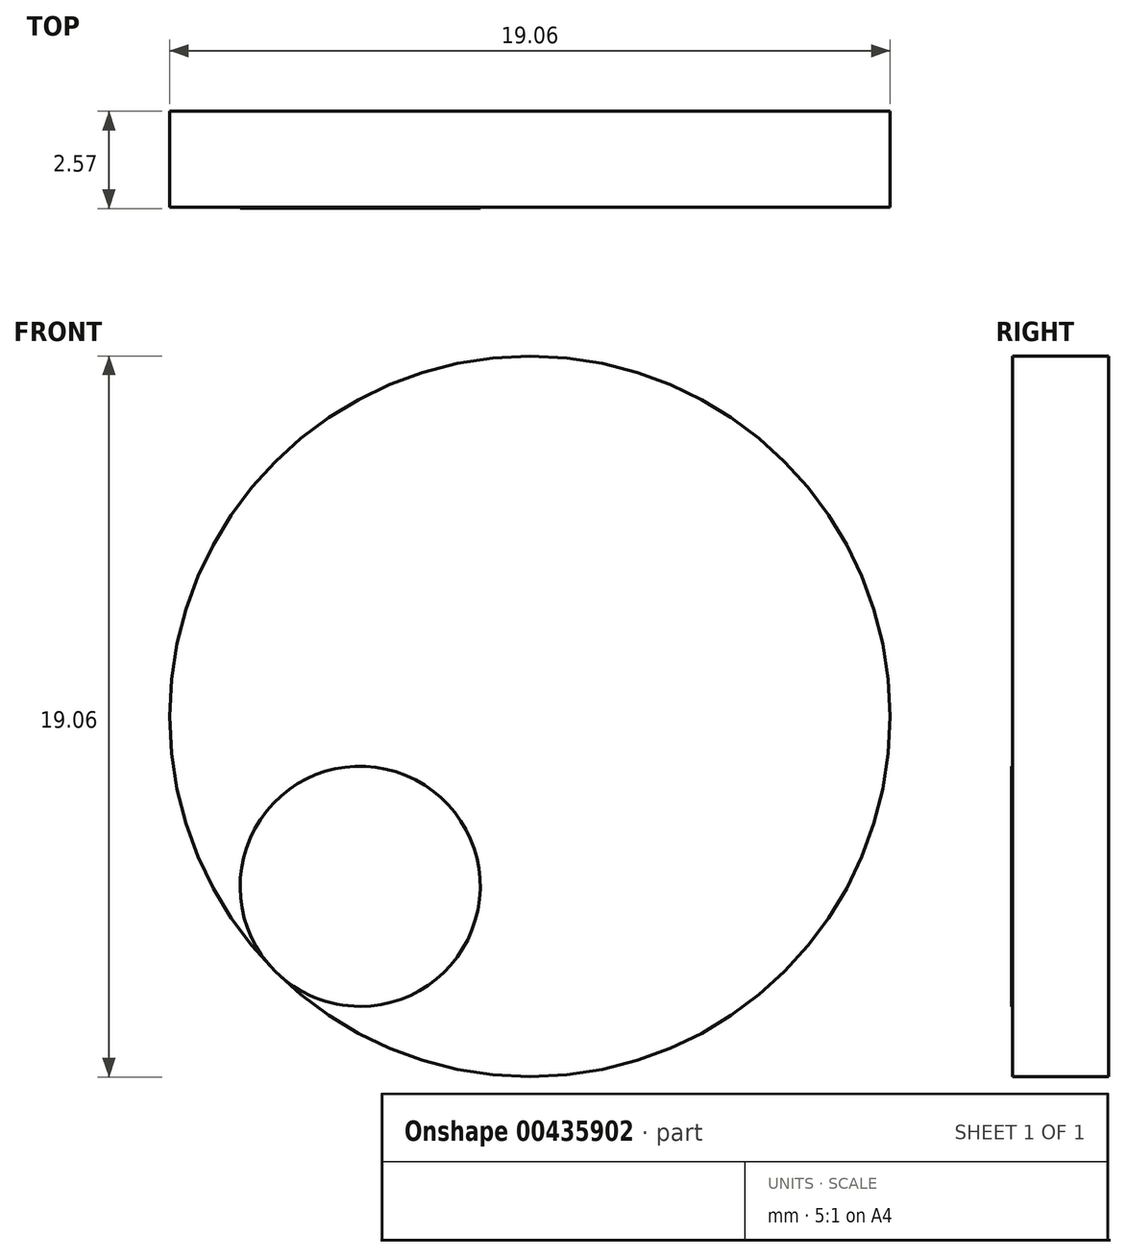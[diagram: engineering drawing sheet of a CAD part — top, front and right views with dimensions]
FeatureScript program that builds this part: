
annotation { "Feature Type Name" : "Feature", "Feature Type Description" : "" }
export const myFeature = defineFeature(function(context is Context, id is Id, definition is map)
    precondition{}
    {
        {
            var Q0;
            Q0=qCreatedBy(makeId("Front.planeOp"),FACE);
            var sketch = newSketch(context, id + "F0", { "sketchPlane" : qUnion([Q0])});
            skCircle(sketch, "E0", {"center": v(0, 0) * mm, "radius": 9.53 * mm});
            skSolve(sketch);
        }
        {
            var Q0;
            Q0=makeQuery(id+"F0.imprint","IMPRINT",FACE,{"disambiguationData":[TD([[makeQuery(id+"F0.imprint","IMPRINT",EDGE,{"derivedFrom":sQuery(id+"F0.wireOp",EDGE,"E0")}),1.0]])]});
            extrude(context, id + "F1", {"entities" : qUnion([Q0]), "depth" : 2.54 * mm});
        }
        {
            var Q0;
            Q0=makeQuery(id+"F1.opExtrude","CAP_FACE",FACE,{"disambiguationData":[OSD([sQuery(id+"F0.wireOp",EDGE,"E0")])],"isStart":false});
            var sketch = newSketch(context, id + "F2", { "sketchPlane" : qUnion([Q0])});
            skCircle(sketch, "E1", {"center": v(-4.5, -4.5) * mm, "radius": 3.18 * mm});
            skLineSegment(sketch, "E2", {"start": v(0, 0) * mm, "end": v(-6.74, -6.74) * mm, "construction": true});
            skSolve(sketch);
        }
        {
            var Q0;
            Q0 = qSketchRegion(id + "F2", true);
            extrude(context, id + "F3", {"entities" : qUnion([Q0]), "operationType" : NewBodyOperationType.ADD, "depth" : 0.03 * mm});
        }
    });
